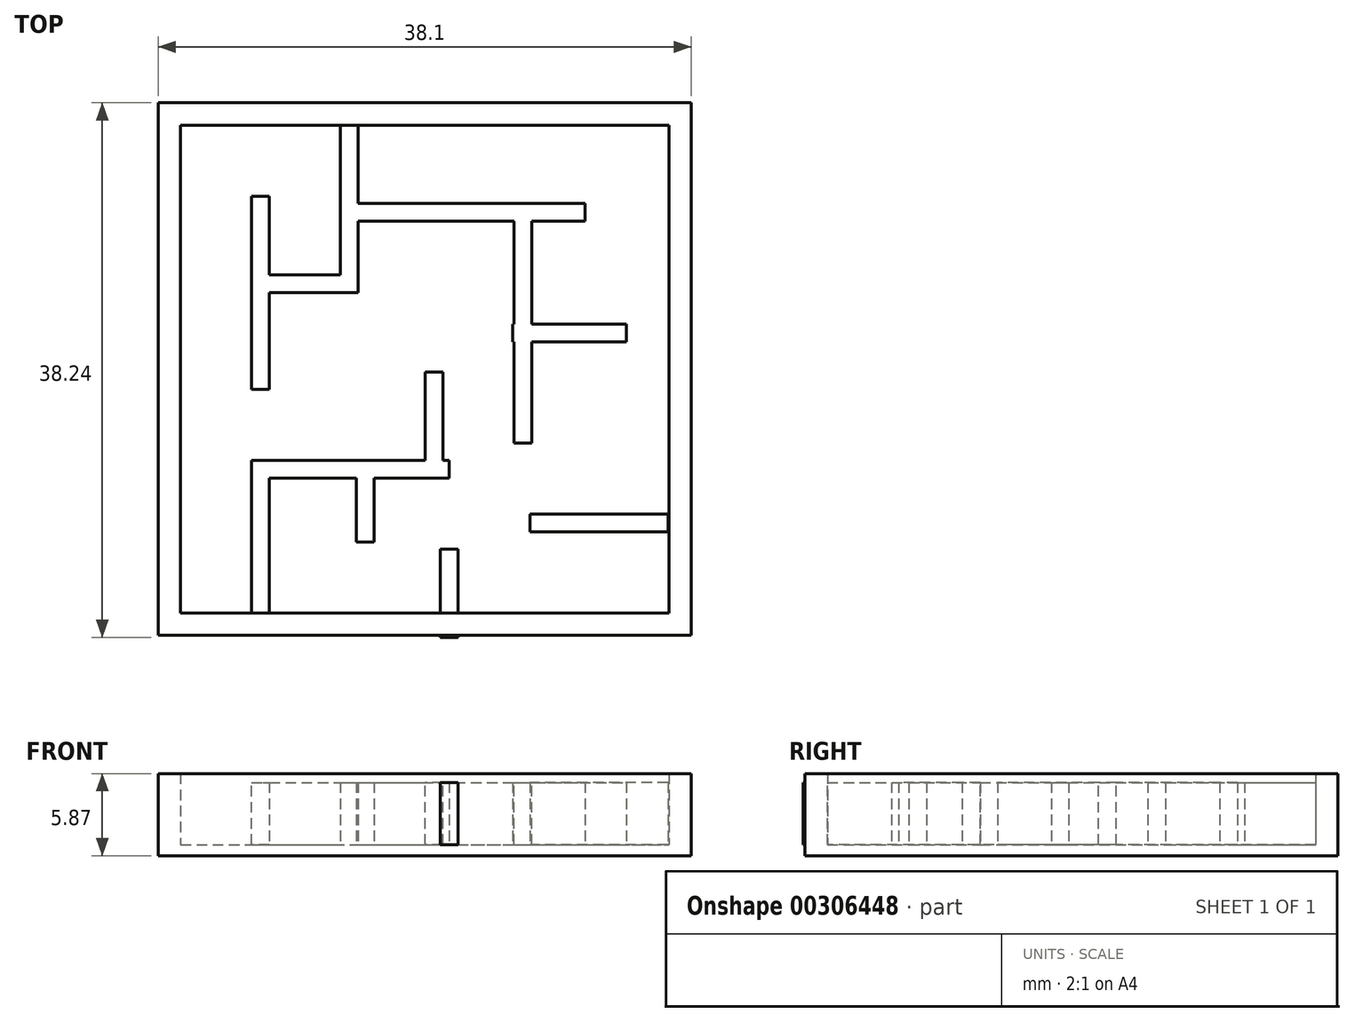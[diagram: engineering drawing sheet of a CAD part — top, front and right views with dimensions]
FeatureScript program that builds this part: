
annotation { "Feature Type Name" : "Feature", "Feature Type Description" : "" }
export const myFeature = defineFeature(function(context is Context, id is Id, definition is map)
    precondition{}
    {
        {
            var Q0;
            Q0=qCreatedBy(makeId("Top.planeOp"),FACE);
            var sketch = newSketch(context, id + "F0", { "sketchPlane" : qUnion([Q0])});
            skLineSegment(sketch, "E0.bottom", {"start": v(-18.14, 15.4) * mm, "end": v(19.96, 15.4) * mm});
            skLineSegment(sketch, "E0.top", {"start": v(-18.14, -22.7) * mm, "end": v(19.96, -22.7) * mm});
            skLineSegment(sketch, "E0.left", {"start": v(-18.14, 15.4) * mm, "end": v(-18.14, -22.7) * mm});
            skLineSegment(sketch, "E0.right", {"start": v(19.96, 15.4) * mm, "end": v(19.96, -22.7) * mm});
            skSolve(sketch);
        }
        {
            var Q0;
            Q0 = qSketchRegion(id + "F0", true);
            extrude(context, id + "F1", {"entities" : qUnion([Q0]), "depth" : 0.8 * mm});
        }
        {
            var Q0;
            Q0=makeQuery(id+"F1.opExtrude","CAP_FACE",FACE,{"disambiguationData":[OSD([sQuery(id+"F0.wireOp",EDGE,"E0.bottom"),sQuery(id+"F0.wireOp",EDGE,"E0.top"),sQuery(id+"F0.wireOp",EDGE,"E0.left"),sQuery(id+"F0.wireOp",EDGE,"E0.right")])],"isStart":false});
            var sketch = newSketch(context, id + "F2", { "sketchPlane" : qUnion([Q0])});
            skLineSegment(sketch, "E1.0", {"start": v(-16.54, 13.8) * mm, "end": v(18.36, 13.8) * mm});
            skLineSegment(sketch, "E1.1", {"start": v(-16.54, 13.8) * mm, "end": v(-16.54, -21.1) * mm});
            skLineSegment(sketch, "E1.2", {"start": v(-16.54, -21.1) * mm, "end": v(18.36, -21.1) * mm});
            skLineSegment(sketch, "E1.3", {"start": v(18.36, 13.8) * mm, "end": v(18.36, -21.1) * mm});
            skSolve(sketch);
        }
        {
            var Q0;
            Q0=makeQuery(id+"F2.imprint","IMPRINT",FACE,{"disambiguationData":[TD([[makeQuery(id+"F2.imprint","IMPRINT",EDGE,{"derivedFrom":sQuery(id+"F2.wireOp",EDGE,"E1.0")}),1.0]])]});
            extrude(context, id + "F3", {"entities" : qUnion([Q0]), "operationType" : NewBodyOperationType.ADD, "depth" : 5.08 * mm});
        }
        {
            var Q0;
            Q0=makeQuery(id+"F2.imprint","IMPRINT",FACE,{"disambiguationData":[TD([[makeQuery(id+"F2.imprint","IMPRINT",EDGE,{"derivedFrom":sQuery(id+"F2.wireOp",EDGE,"E1.0")}),-1.0]])]});
            var sketch = newSketch(context, id + "F4", { "sketchPlane" : qUnion([Q0])});
            skLineSegment(sketch, "E2.bottom", {"start": v(-11.46, -21.18) * mm, "end": v(-10.2, -21.18) * mm});
            skLineSegment(sketch, "E2.top", {"start": v(-11.46, -10.19) * mm, "end": v(-10.2, -10.19) * mm});
            skLineSegment(sketch, "E2.left", {"start": v(-11.46, -21.18) * mm, "end": v(-11.46, -10.19) * mm});
            skLineSegment(sketch, "E2.right", {"start": v(-10.2, -21.18) * mm, "end": v(-10.2, -10.19) * mm});
            skLineSegment(sketch, "E3.bottom", {"start": v(-10.2, -5.1) * mm, "end": v(-11.46, -5.1) * mm});
            skLineSegment(sketch, "E3.top", {"start": v(-10.2, 8.71) * mm, "end": v(-11.46, 8.71) * mm});
            skLineSegment(sketch, "E3.left", {"start": v(-10.2, -5.1) * mm, "end": v(-10.2, 8.71) * mm});
            skLineSegment(sketch, "E3.right", {"start": v(-11.46, -5.1) * mm, "end": v(-11.46, 8.71) * mm});
            skPoint(sketch, "E4.oppositeSnap0", {"position": v(-10.2, 1.8) * mm});
            skLineSegment(sketch, "E4.bottom", {"start": v(-10.2, 3.07) * mm, "end": v(-3.84, 3.07) * mm});
            skLineSegment(sketch, "E4.top", {"start": v(-10.2, 1.8) * mm, "end": v(-3.84, 1.8) * mm});
            skLineSegment(sketch, "E4.left", {"start": v(-10.2, 3.07) * mm, "end": v(-10.2, 1.8) * mm});
            skLineSegment(sketch, "E4.right", {"start": v(-3.84, 3.07) * mm, "end": v(-3.84, 1.8) * mm});
            skLineSegment(sketch, "E5.bottom", {"start": v(-5.11, 3.07) * mm, "end": v(-3.84, 3.07) * mm});
            skLineSegment(sketch, "E5.top", {"start": v(-5.11, 13.8) * mm, "end": v(-3.84, 13.8) * mm});
            skLineSegment(sketch, "E5.left", {"start": v(-5.11, 3.07) * mm, "end": v(-5.11, 13.8) * mm});
            skLineSegment(sketch, "E5.right", {"start": v(-3.84, 3.07) * mm, "end": v(-3.84, 13.8) * mm});
            skSolve(sketch);
        }
        {
            var Q0;
            Q0 = qSketchRegion(id + "F4", true);
            var Q1;
            Q1 = qSketchRegion(id + "F7", true);
            extrude(context, id + "F5", {"entities" : qUnion([Q0, Q1]), "operationType" : NewBodyOperationType.ADD, "depth" : 4.44 * mm});
        }
        {
            var Q0;
            Q0=makeQuery(id+"F2.imprint","IMPRINT",FACE,{"disambiguationData":[TD([[makeQuery(id+"F2.imprint","IMPRINT",EDGE,{"derivedFrom":sQuery(id+"F2.wireOp",EDGE,"E1.0")}),-1.0]])]});
            var sketch = newSketch(context, id + "F6", { "sketchPlane" : qUnion([Q0])});
            skSolve(sketch);
        }
        {
            var Q0;
            Q0=makeQuery(id+"F2.imprint","IMPRINT",FACE,{"disambiguationData":[TD([[makeQuery(id+"F2.imprint","IMPRINT",EDGE,{"derivedFrom":sQuery(id+"F2.wireOp",EDGE,"E1.0")}),-1.0]])]});
            var sketch = newSketch(context, id + "F7", { "sketchPlane" : qUnion([Q0])});
            skLineSegment(sketch, "E6.bottom", {"start": v(-10.64, -10.2) * mm, "end": v(2.66, -10.2) * mm});
            skLineSegment(sketch, "E6.top", {"start": v(-10.64, -11.47) * mm, "end": v(-4, -11.47) * mm});
            skLineSegment(sketch, "E6.left", {"start": v(-10.64, -10.2) * mm, "end": v(-10.64, -11.47) * mm});
            skLineSegment(sketch, "E6.right", {"start": v(2.66, -10.2) * mm, "end": v(2.66, -11.47) * mm});
            skLineSegment(sketch, "E7.top", {"start": v(-4, -16.03) * mm, "end": v(-2.72, -16.03) * mm});
            skLineSegment(sketch, "E7.left", {"start": v(-4, -11.47) * mm, "end": v(-4, -16.03) * mm});
            skLineSegment(sketch, "E7.right", {"start": v(-2.72, -11.47) * mm, "end": v(-2.72, -16.03) * mm});
            skLineSegment(sketch, "E8.bottom", {"start": v(2.01, -22.85) * mm, "end": v(3.28, -22.85) * mm});
            skLineSegment(sketch, "E8.top", {"start": v(2.01, -16.55) * mm, "end": v(3.28, -16.55) * mm});
            skLineSegment(sketch, "E8.left", {"start": v(2.01, -22.85) * mm, "end": v(2.01, -16.55) * mm});
            skLineSegment(sketch, "E8.right", {"start": v(3.28, -22.85) * mm, "end": v(3.28, -16.55) * mm});
            skLineSegment(sketch, "E9.trimOffspring", {"start": v(-2.72, -11.47) * mm, "end": v(2.66, -11.47) * mm});
            skSolve(sketch);
        }
        {
            var Q0;
            Q0=makeQuery(id+"F7.imprint","IMPRINT",FACE,{"disambiguationData":[TD([[makeQuery(id+"F7.imprint","IMPRINT",EDGE,{"derivedFrom":sQuery(id+"F7.wireOp",EDGE,"E6.bottom")}),1.0]])]});
            var sketch = newSketch(context, id + "F8", { "sketchPlane" : qUnion([Q0])});
            skLineSegment(sketch, "E10.bottom", {"start": v(2.2, -11) * mm, "end": v(0.93, -11) * mm});
            skLineSegment(sketch, "E10.top", {"start": v(2.2, -3.87) * mm, "end": v(0.93, -3.87) * mm});
            skLineSegment(sketch, "E10.left", {"start": v(2.2, -11) * mm, "end": v(2.2, -3.87) * mm});
            skLineSegment(sketch, "E10.right", {"start": v(0.93, -11) * mm, "end": v(0.93, -3.87) * mm});
            skLineSegment(sketch, "E11.bottom", {"start": v(-4.46, 8.2) * mm, "end": v(12.36, 8.2) * mm});
            skLineSegment(sketch, "E11.top", {"start": v(-4.46, 6.92) * mm, "end": v(12.36, 6.92) * mm});
            skLineSegment(sketch, "E11.left", {"start": v(-4.46, 8.2) * mm, "end": v(-4.46, 6.92) * mm});
            skLineSegment(sketch, "E11.right", {"start": v(12.36, 8.2) * mm, "end": v(12.36, 6.92) * mm});
            skLineSegment(sketch, "E12.bottom", {"start": v(7.28, 6.92) * mm, "end": v(8.55, 6.92) * mm});
            skLineSegment(sketch, "E12.top", {"start": v(7.28, -8.94) * mm, "end": v(8.55, -8.94) * mm});
            skLineSegment(sketch, "E12.left", {"start": v(7.28, 6.92) * mm, "end": v(7.28, -8.94) * mm});
            skLineSegment(sketch, "E12.right", {"start": v(8.55, 6.92) * mm, "end": v(8.55, -8.94) * mm});
            skLineSegment(sketch, "E13.bottom", {"start": v(18.3, -15.3) * mm, "end": v(8.44, -15.3) * mm});
            skLineSegment(sketch, "E13.top", {"start": v(18.3, -14.02) * mm, "end": v(8.44, -14.02) * mm});
            skLineSegment(sketch, "E13.left", {"start": v(18.3, -15.3) * mm, "end": v(18.3, -14.02) * mm});
            skLineSegment(sketch, "E13.right", {"start": v(8.44, -15.3) * mm, "end": v(8.44, -14.02) * mm});
            skSolve(sketch);
        }
        {
            var Q0;
            Q0 = qSketchRegion(id + "F7", true);
            extrude(context, id + "F9", {"entities" : qUnion([Q0]), "operationType" : NewBodyOperationType.ADD, "depth" : 4.44 * mm});
        }
        {
            var Q0;
            Q0 = qSketchRegion(id + "F8", true);
            extrude(context, id + "F10", {"entities" : qUnion([Q0]), "operationType" : NewBodyOperationType.ADD, "depth" : 4.44 * mm});
        }
        {
            var Q0;
            Q0=makeQuery(id+"F6.imprint","IMPRINT",FACE,{"disambiguationData":[TD([[makeQuery(id+"F6.imprint","IMPRINT",EDGE,{"derivedFrom":makeQuery(id+"F2.imprint","IMPRINT",EDGE,{"derivedFrom":sQuery(id+"F2.wireOp",EDGE,"E1.0")})}),-1.0]])]});
            var sketch = newSketch(context, id + "F11", { "sketchPlane" : qUnion([Q0])});
            skLineSegment(sketch, "E14.bottom", {"start": v(7.18, -0.46) * mm, "end": v(15.31, -0.46) * mm});
            skLineSegment(sketch, "E14.top", {"start": v(7.18, -1.73) * mm, "end": v(15.31, -1.73) * mm});
            skLineSegment(sketch, "E14.left", {"start": v(7.18, -0.46) * mm, "end": v(7.18, -1.73) * mm});
            skLineSegment(sketch, "E14.right", {"start": v(15.31, -0.46) * mm, "end": v(15.31, -1.73) * mm});
            skSolve(sketch);
        }
        {
            var Q0;
            Q0 = qSketchRegion(id + "F11", true);
            extrude(context, id + "F12", {"entities" : qUnion([Q0]), "operationType" : NewBodyOperationType.ADD, "depth" : 4.44 * mm});
        }
    });
